# Revit family: KG110 - Kick Plate
name_source: partatom
category: Specialty Equipment
units: mm (PartAtom-declared; Revit-internal decimal feet)

## family parameters
Always vertical = No
Cut with Voids When Loaded = No
Part Type = Normal
Room Calculation Point = No
Round Connector Dimension = Use Diameter
Shared = No
Work Plane-Based = No

## types (1)
- KG110 - Kick Plate
    AssetType = Fixed
    BIMObjectName = KingswayGroup_KickPlates_KickPlate
    Category = Pr_30_36_33_45:Kick plates
    Color = For full range of available finishes and colours, contact Kingsway Group
    Default Elevation = 0 mm  [stored 0 ft]
    Description = Kick Plate
    DurationUnit = year
    Features = A highly durable Kick Plate manufactured from stainless steel sheet to exact dimensions to suit specific door widths
    Finish = For full range of available finishes and colours, contact Kingsway Group
    IfcExportAs = IfcDiscreteAccessoryType
    IfcExportType = USERDEFINED
    Manufacturer = Kingsway Group
    ManufacturerName = Kingsway Group
    ManufacturerURL = https://kingswaygroupglobal.com
    Material = Stainless Steel
    Model = KG110
    ModelNumber = KG110
    ModelReference = Kick Plate
    Name = KickPlates_KickPlate_KG110_KingswayGroup
    NominalHeight = 200 mm  [stored 0.656168 ft]
    NominalLength = 1000 mm  [stored 3.28084 ft]
    NominalWidth = 2 mm  [stored 0.00656168 ft]
    PlateMaterial = NBS_Concept
    ProductInformation = https://kingswaygroupglobal.com
    Size = 1000 x 200 x 1.5 mm
    URL = https://kingswaygroupglobal.com
    Uniclass2015Code = Pr_30_36_33_45
    Uniclass2015Title = Kick plates
    Uniclass2015Version = Products v1.36
    Version = 1
    WarrantyDescription = 5-Year Guarantee *For faulty manufacture and not for damage
    WarrantyDurationParts = 5
    WarrantyDurationUnit = year

note: [stored X ft] marks values corroborated as IEEE doubles in the binary element streams (Revit-internal decimal feet)

## geometry (parser evidence)
native form markers: Sweep x3
no freeform markers — native parametric forms only
